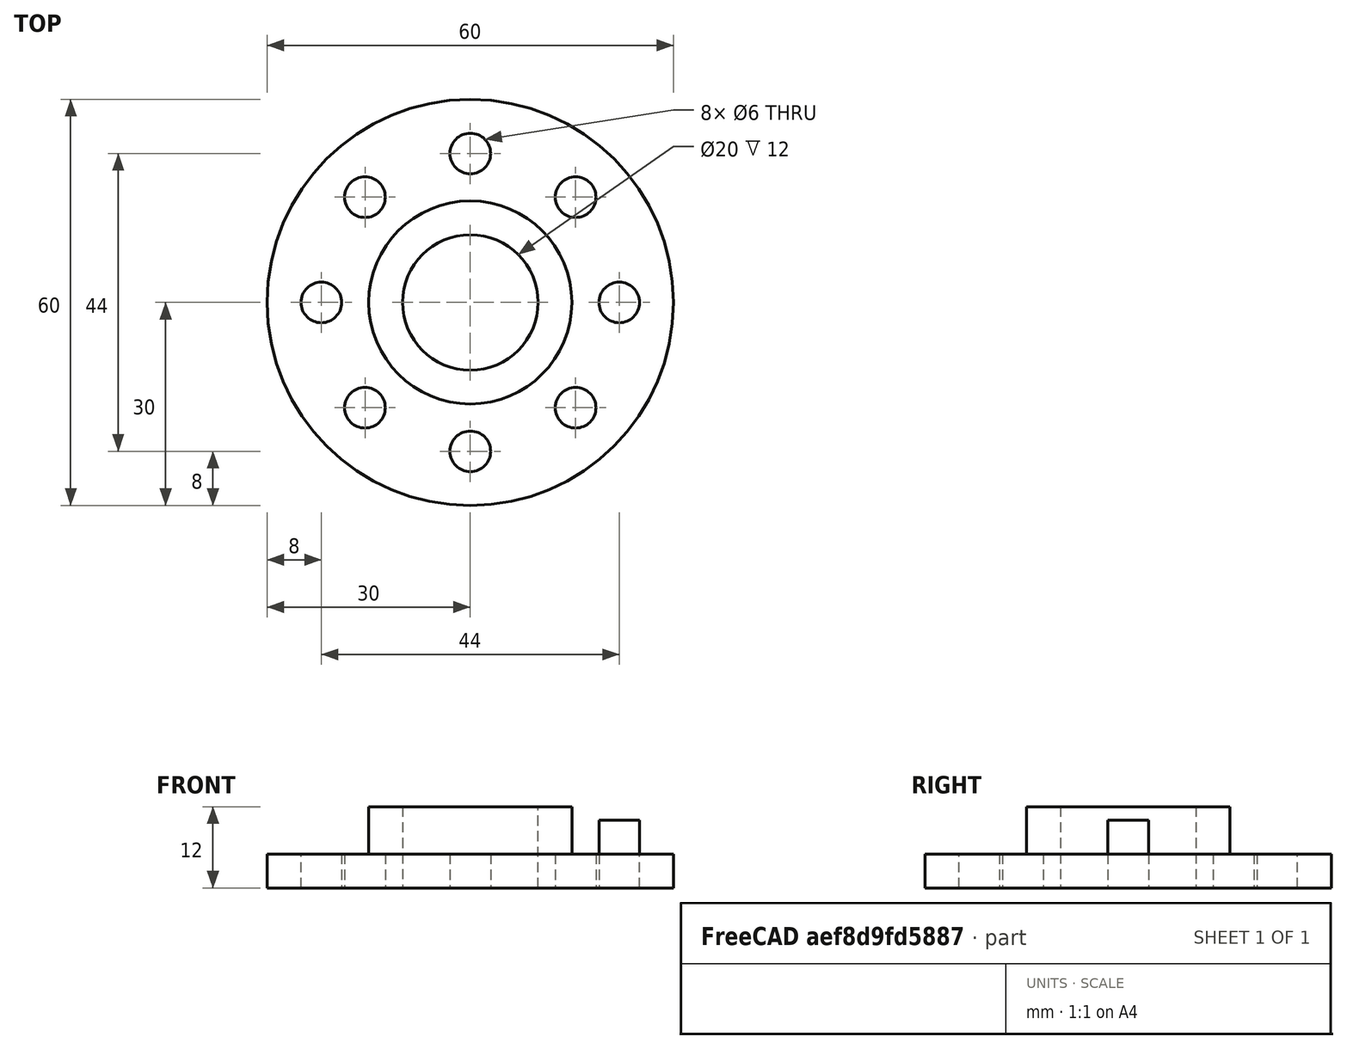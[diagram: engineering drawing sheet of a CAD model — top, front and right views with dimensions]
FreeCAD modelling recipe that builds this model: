
FCSTD DOCUMENT  (FreeCAD 0.20R29177 (Git))
Label: Video11
License: All rights reserved
LicenseURL: http://en.wikipedia.org/wiki/All_rights_reserved
objects: Part::Cylinder×4, Part::Cut×2, Part::Fuse×1, Part::FeaturePython×1
note: 7 computed .brp shape members not serialized (recipe doc carries the construction recipe); baked Part::Feature solids carry a one-line shape summary decoded from their .brp

FEATURE [Part::Cylinder] Cylinder  label="Base"
  Angle = 360
  AttacherType = Attacher::AttachEngine3D
  FirstAngle = 0
  Height = 5
  Radius = 30
  SecondAngle = 0
FEATURE [Part::Cylinder] Cylinder001  label="Tubo_ext"
  Angle = 360
  AttacherType = Attacher::AttachEngine3D
  FirstAngle = 0
  Height = 12
  Radius = 15
  SecondAngle = 0
FEATURE [Part::Fuse] Fusion
  Base = -> Cylinder
  Tool = -> Cylinder001
FEATURE [Part::Cylinder] Cylinder002  label="Tubo_int"
  Angle = 360
  AttacherType = Attacher::AttachEngine3D
  FirstAngle = 0
  Height = 30
  Placement = pos=(0,0,-1) rot=(0,0,1;0rad)
  Radius = 10
  SecondAngle = 0
FEATURE [Part::Cut] Cut  label="Brida sin taladros"
  Base = -> Fusion
  Tool = -> Cylinder002
FEATURE [Part::Cylinder] Cylinder003  label="Taladro"
  Angle = 360
  AttacherType = Attacher::AttachEngine3D
  FirstAngle = 0
  Height = 10
  Placement = pos=(22,0,0) rot=(0,0,1;0rad)
  Radius = 3
  SecondAngle = 0
FEATURE [Part::FeaturePython] Array  # Draft array (typed FeaturePython)
  AlwaysSyncPlacement = false
  Angle = 360
  ArrayType = 1
  Axis = (0,0,1)
  Base = -> Cylinder003
  Center = (0,0,0)
  Count = 8
  ExpandArray = false
  Fuse = false
  IntervalAxis = (0,0,0)
  IntervalX = (100,0,0)
  IntervalY = (0,100,0)
  IntervalZ = (0,0,100)
  NumberCircles = 3
  NumberPolar = 8
  NumberX = 2
  NumberY = 2
  NumberZ = 1
  PlacementList = 8 placements: [(22,0,0),(15.5563,15.5563,0),(3.55271e-15,22,0),(-15.5563,15.5563,0),(-22,2.69422e-15,0),(-15.5563,-15.5563,0),(-3.55271e-15,-22,0),(15.5563,-15.5563,0)]
  RadialDistance = 50
  ScaleList = (8) [(1,1,1),(1,1,1),(1,1,1),(1,1,1),(1,1,1),(1,1,1),(1,1,1),(1,1,1)]
  Symmetry = 1
  TangentialDistance = 25
FEATURE [Part::Cut] Cut001  label="Brida"
  Base = -> Cut
  Tool = -> Array
